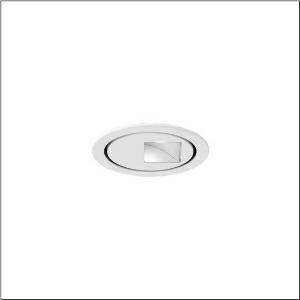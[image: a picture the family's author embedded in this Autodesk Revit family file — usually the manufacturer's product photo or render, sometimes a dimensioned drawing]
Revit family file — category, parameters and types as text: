
# Revit family: lunis_11_micro_round_51dj11cd1wf21
name_source: partatom
category: Lighting Fixtures
units: mm (PartAtom-declared; Revit-internal decimal feet)

## family parameters
Cut with Voids When Loaded = No
Host = Face
Light Source = No
Part Type = Normal
Room Calculation Point = No
Round Connector Dimension = Use Diameter
Shared = No

## types (1)
- Lunis 11 micro round (1 x LED 3000K / CRI = 80 (unbekannt), 1320 lm, 3000K)
    Apparent Load = 20 VA
    CIE Flux Codes = 42 75 96 100 100
    Color Rendering = 80
    Color Temperature = 3000K
    Default Elevation = 1800 mm
    Description = Lunis 11 micro round, downlight, light control with wallwasher, of highly reflective aluminium, highly specular, light emission: direct distribution, LED rated luminous flux: 1.320lm, light colour: 830, with terminal, 5-pole, mains connection: 220..230V, AC, 50/60Hz, LED module, of aluminium, highly specular, white, diameter: 114mm, clamping range: 1..40mm, recessing ring, of plastic, traffic white (RAL 9016), protection rating (complete): IP20, insulation class (complete): insulation class II (safety insulation), certification: CE, permissible ambient temperature for indoor applications: 0..+35°C, packaging unit: 1 piece
    Height = 0 mm  [stored 0 ft]
    Lamp = 1 x LED 3000K / CRI >= 80 (unbekannt)
    Lamp Light Flux = 1320 lm
    Lamp count = 1
    Length = 114 mm
    Luminous efficacy = 67 lm/W
    Manufacturer = Siteco
    ModVariant = No
    Model = 51DJ11CD1WF21
    Mounting Place = Ceiling
    Mounting Type = Recessed
    Number of Poles = 1
    OnlyDefault = Yes
    Power Factor = 1
    Product Name = Lunis 11 micro round
    Product group = downlight
    ProductGroupID = 401
    Protection Class = Protection class II
    Protection Degree = IP 20
    RLX_Detail_Level = 1
    RLX_Emergency_Light_Flux = 0 lm
    RLX_Emergency_Type = 0
    RLX_Emergency_Type_DB = No
    RlxData = <blob elided: 40405 chars, md5=8b72c787>
    Socket = socket
    Standby Power = 0 W
    System Light Flux = 1320 lm
    System Power = 20 W
    Type Comments = Product without accessories
    Type Image = l_1004773.jpg
    URL = http://relux.com
    VarID = ---
    Voltage = 0 V
    Weight = 0.00 kg
    Width = 114 mm

note: [stored X ft] marks values corroborated as IEEE doubles in the binary element streams (Revit-internal decimal feet)

## geometry (parser evidence)
native form markers: Blend x4, Sweep x11
no freeform markers — native parametric forms only
